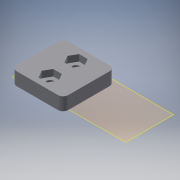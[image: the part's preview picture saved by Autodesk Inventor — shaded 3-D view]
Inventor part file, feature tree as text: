
AUTODESK INVENTOR PART (.ipt)
format: ipt  version: 2016 (Build 200138000, 138)  size: 149,504 bytes
history: native  units: mm
features: sketch x3, extrude x2, reference x2, plane x1, fillet x1, hole x1, projected_geometry x1
ambient origin geometry x8: Origin, YZ Plane, XZ Plane, XY Plane, X Axis, Y Axis, Z Axis, Center Point
bodies: Solid1 (feature_tree)
feature tree (11):
  plane  "Work Plane1"
  extrude  "Extrusion1"  Depth=20.0mm
  fillet  "Fillet1"  Radius=5.0mm
  hole  "Hole1"  [1 undecoded]
  extrude  "Extrusion2"  Depth=5.7mm
  sketch  "Sketch1"  dims[d0=20.0mm d1=20.0mm d2=5.0mm d3=0.0mm]
  reference  "Reference1"
  sketch  "Sketch2"  dims[d4=2.0mm d5=5.0mm]
  reference  "Reference2"
  projected_geometry  "Projected Loop1"
  sketch  "Sketch3"  dims[d6=10.0mm d7=3.0mm d8=6.0mm d9=4.0mm d10=2.0mm d11=90.0deg d12=8.0mm d13=20.594885mm d14=5.7mm d15=2.5mm d16=0.0mm]
note: 1 required parameter value undecoded (feature->parameter linkage not recoverable at this tier; creation-order binding heuristic only, values carry confidence <= 0.55)
